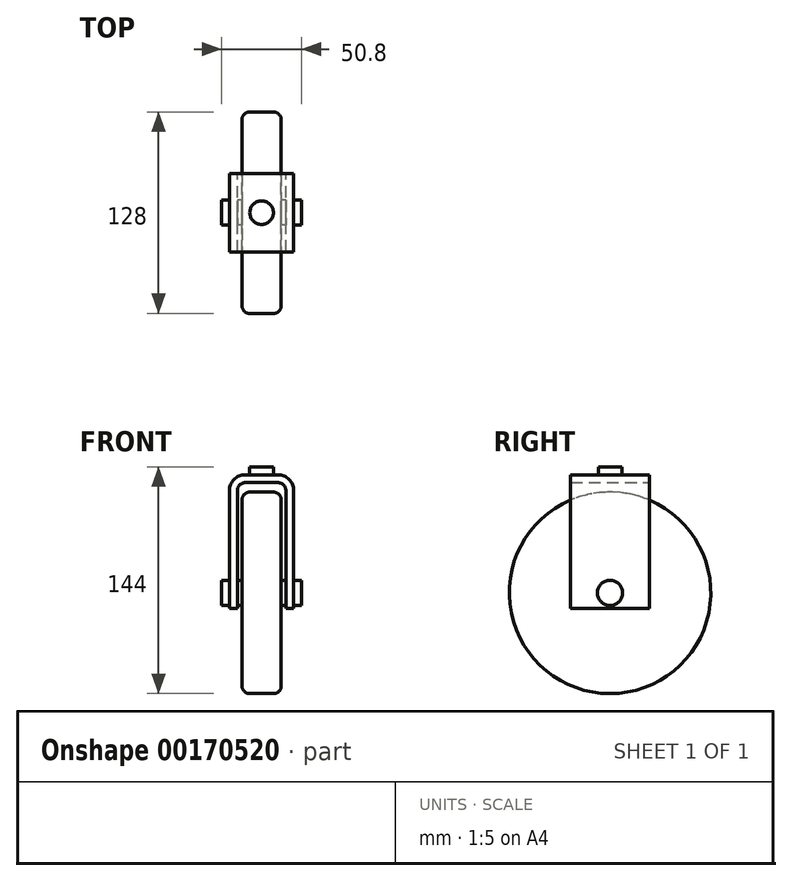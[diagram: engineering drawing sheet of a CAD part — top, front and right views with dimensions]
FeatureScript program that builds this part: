
annotation { "Feature Type Name" : "Feature", "Feature Type Description" : "" }
export const myFeature = defineFeature(function(context is Context, id is Id, definition is map)
    precondition{}
    {
        {
            var Q0;
            Q0=qCreatedBy(makeId("Front.planeOp"),FACE);
            var sketch = newSketch(context, id + "F0", { "sketchPlane" : qUnion([Q0])});
            skLineSegment(sketch, "E0", {"start": v(-87.22, 0) * mm, "end": v(73.7, 0) * mm, "construction": true});
            skLineSegment(sketch, "E1.bottom", {"start": v(-25.4, 8) * mm, "end": v(-20.4, 8) * mm});
            skLineSegment(sketch, "E1.top", {"start": v(-25.4, 0) * mm, "end": v(25.4, 0) * mm});
            skLineSegment(sketch, "E1.left", {"start": v(-25.4, 8) * mm, "end": v(-25.4, 0) * mm});
            skLineSegment(sketch, "E1.right", {"start": v(25.4, 8) * mm, "end": v(25.4, 0) * mm});
            skLineSegment(sketch, "E2.bottom", {"start": v(-7.5, 64) * mm, "end": v(7.5, 64) * mm});
            skLineSegment(sketch, "E2.top", {"start": v(-12.5, 0) * mm, "end": v(12.5, 0) * mm});
            skLineSegment(sketch, "E2.left", {"start": v(-12.5, 59) * mm, "end": v(-12.5, 8) * mm});
            skLineSegment(sketch, "E2.right", {"start": v(12.5, 59) * mm, "end": v(12.5, 8) * mm});
            skLineSegment(sketch, "E3", {"start": v(0, 0) * mm, "end": v(0, 77.8) * mm, "construction": true});
            skPoint(sketch, "E3.endSnap0", {"position": v(0, 64) * mm});
            skPoint(sketch, "E4.visualSharp", {"position": v(-12.5, 64) * mm});
            skArc(sketch, "E4.filletArc", {"start": v(-7.5, 64) * mm, "mid": v(-11.04, 62.54) * mm, "end": v(-12.5, 59) * mm});
            skPoint(sketch, "E5.visualSharp", {"position": v(12.5, 64) * mm});
            skArc(sketch, "E5.filletArc", {"start": v(12.5, 59) * mm, "mid": v(11.04, 62.54) * mm, "end": v(7.5, 64) * mm});
            skLineSegment(sketch, "E6.0", {"start": v(-15.4, 8) * mm, "end": v(-15.4, 5) * mm});
            skLineSegment(sketch, "E7.0", {"start": v(15.4, 8) * mm, "end": v(15.4, 5) * mm});
            skLineSegment(sketch, "E8.0", {"start": v(-20.4, 8) * mm, "end": v(-20.4, 5) * mm});
            skLineSegment(sketch, "E9.0", {"start": v(20.4, 8) * mm, "end": v(20.4, 5) * mm});
            skLineSegment(sketch, "E10.0", {"start": v(-20.4, 5) * mm, "end": v(-15.4, 5) * mm});
            skLineSegment(sketch, "E11.trimOffspring", {"start": v(15.4, 5) * mm, "end": v(20.4, 5) * mm});
            skLineSegment(sketch, "E12.trimOffspring", {"start": v(20.4, 8) * mm, "end": v(25.4, 8) * mm});
            skLineSegment(sketch, "E13.trimOffspring", {"start": v(-15.4, 8) * mm, "end": v(-12.5, 8) * mm});
            skLineSegment(sketch, "E14.trimOffspring", {"start": v(12.5, 8) * mm, "end": v(15.4, 8) * mm});
            skSolve(sketch);
        }
        {
            var Q0;
            Q0=makeQuery(id+"F0.imprint","IMPRINT",FACE,{"disambiguationData":[TD([[makeQuery(id+"F0.imprint","IMPRINT",EDGE,{"derivedFrom":sQuery(id+"F0.wireOp",EDGE,"E1.bottom")}),-1.0]])]});
            var Q1;
            Q1=sQuery(id+"F0.wireOp",EDGE,"E0");
            revolve(context, id + "F1", {"entities" : qUnion([Q0]), "axis" : qUnion([Q1]), "revolveType" : RevolveType.FULL});
        }
        {
            var Q0;
            Q0=qCreatedBy(makeId("Front.planeOp"),FACE);
            var sketch = newSketch(context, id + "F2", { "sketchPlane" : qUnion([Q0])});
            skLineSegment(sketch, "E15", {"start": v(-15.4, -10) * mm, "end": v(-20.4, -10) * mm});
            skLineSegment(sketch, "E16", {"start": v(-20.4, -10) * mm, "end": v(-20.4, 65) * mm});
            skLineSegment(sketch, "E17", {"start": v(-10.4, 75) * mm, "end": v(0, 75) * mm});
            skLineSegment(sketch, "E18", {"start": v(-15.4, -10) * mm, "end": v(-15.4, 65) * mm});
            skLineSegment(sketch, "E19.0", {"start": v(-10.4, 70) * mm, "end": v(0, 70) * mm});
            skArc(sketch, "E20.filletArc", {"start": v(-10.4, 70) * mm, "mid": v(-13.94, 68.54) * mm, "end": v(-15.4, 65) * mm});
            skArc(sketch, "E21.0", {"start": v(-10.4, 75) * mm, "mid": v(-17.47, 72.07) * mm, "end": v(-20.4, 65) * mm});
            skLineSegment(sketch, "E22", {"start": v(0, 82.5) * mm, "end": v(0, -89.77) * mm, "construction": true});
            skArc(sketch, "E23.MirrorCS", {"start": v(10.4, 70) * mm, "mid": v(13.94, 68.54) * mm, "end": v(15.4, 65) * mm});
            skLineSegment(sketch, "E24.MirrorCS", {"start": v(15.4, -10) * mm, "end": v(20.4, -10) * mm});
            skArc(sketch, "E25.MirrorCS", {"start": v(10.4, 75) * mm, "mid": v(17.47, 72.07) * mm, "end": v(20.4, 65) * mm});
            skLineSegment(sketch, "E26.MirrorCS", {"start": v(15.4, -10) * mm, "end": v(15.4, 65) * mm});
            skLineSegment(sketch, "E27.MirrorCS", {"start": v(10.4, 75) * mm, "end": v(0, 75) * mm});
            skLineSegment(sketch, "E28.MirrorCS", {"start": v(10.4, 70) * mm, "end": v(0, 70) * mm});
            skLineSegment(sketch, "E29.MirrorCS", {"start": v(20.4, -10) * mm, "end": v(20.4, 65) * mm});
            skSolve(sketch);
        }
        {
            var Q0;
            Q0=makeQuery(id+"F2.imprint","IMPRINT",FACE,{"disambiguationData":[TD([[makeQuery(id+"F2.imprint","IMPRINT",EDGE,{"derivedFrom":sQuery(id+"F2.wireOp",EDGE,"E15")}),-1.0]])]});
            extrude(context, id + "F3", {"entities" : qUnion([Q0]), "operationType" : NewBodyOperationType.ADD, "endBound" : BoundingType.SYMMETRIC, "depth" : 50 * mm});
        }
        {
            var Q0;
            Q0=makeQuery(id+"F3.opExtrude","SWEPT_FACE",FACE,{"disambiguationData":[OSD([sQuery(id+"F2.wireOp",EDGE,"E17"),sQuery(id+"F2.wireOp",EDGE,"E27.MirrorCS")])]});
            var sketch = newSketch(context, id + "F4", { "sketchPlane" : qUnion([Q0])});
            skCircle(sketch, "E30", {"center": v(0, 0) * mm, "radius": 7.5 * mm});
            skSolve(sketch);
        }
        {
            var Q0;
            Q0 = qSketchRegion(id + "F4", true);
            extrude(context, id + "F5", {"entities" : qUnion([Q0]), "operationType" : NewBodyOperationType.ADD, "depth" : 5 * mm});
        }
    });
